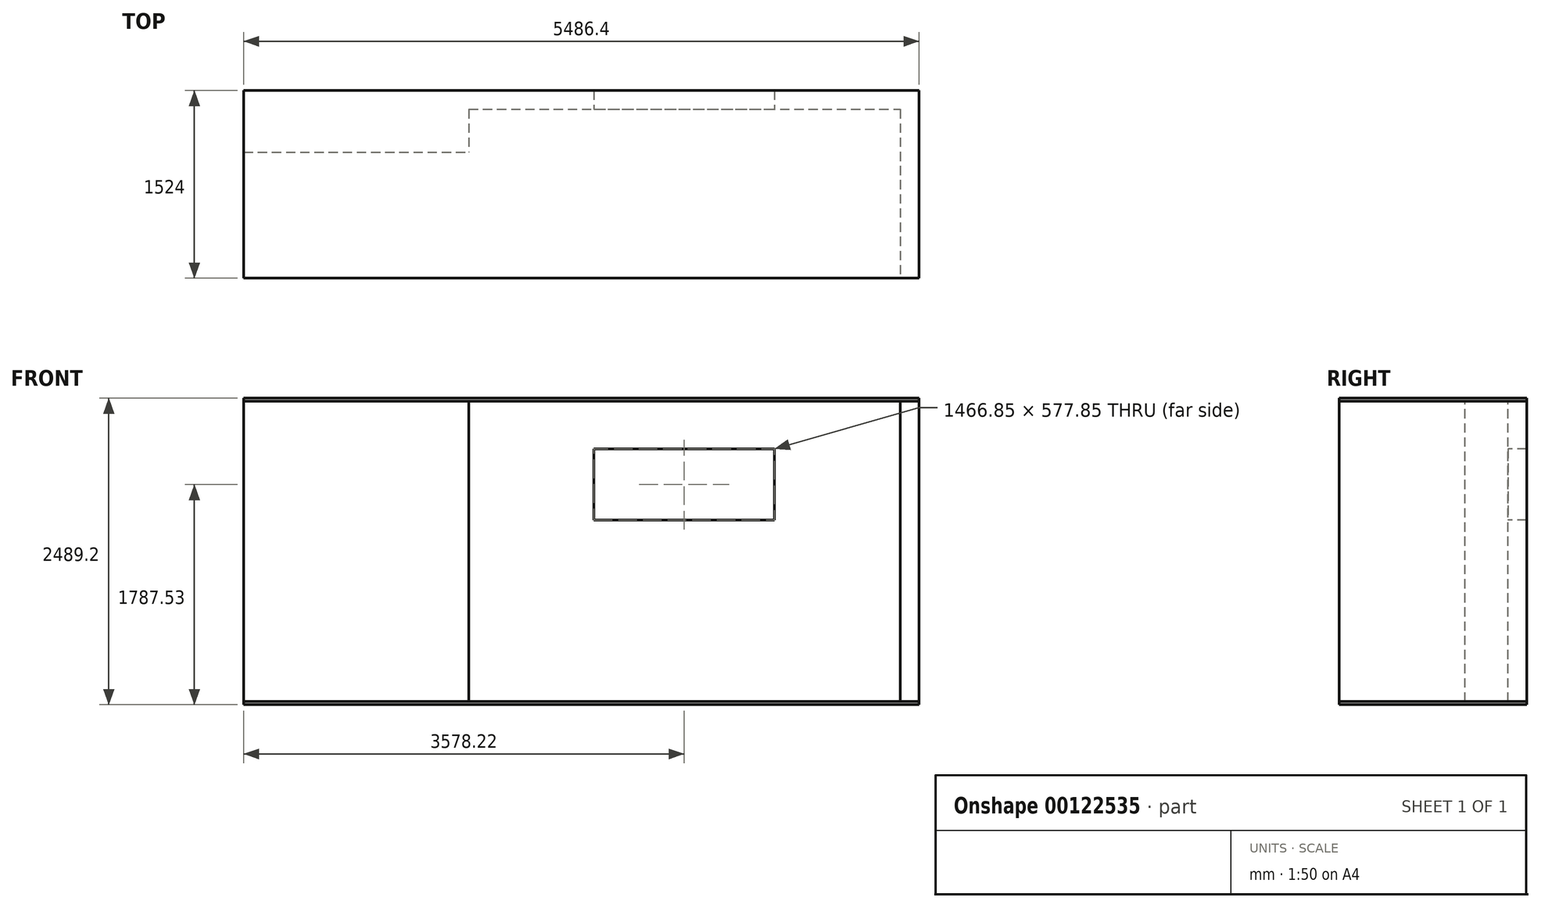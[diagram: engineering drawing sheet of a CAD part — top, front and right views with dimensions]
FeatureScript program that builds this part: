
annotation { "Feature Type Name" : "Feature", "Feature Type Description" : "" }
export const myFeature = defineFeature(function(context is Context, id is Id, definition is map)
    precondition{}
    {
        {
            var Q0;
            Q0=qCreatedBy(makeId("Front.planeOp"),FACE);
            var sketch = newSketch(context, id + "F0", { "sketchPlane" : qUnion([Q0])});
            skLineSegment(sketch, "E0.bottom", {"start": v(0, 0) * mm, "end": v(3505.2, 0) * mm});
            skLineSegment(sketch, "E0.top", {"start": v(0, 2438.4) * mm, "end": v(3505.2, 2438.4) * mm});
            skLineSegment(sketch, "E0.left", {"start": v(0, 0) * mm, "end": v(0, 2438.4) * mm});
            skLineSegment(sketch, "E0.right", {"start": v(3505.2, 0) * mm, "end": v(3505.2, 2438.4) * mm});
            skLineSegment(sketch, "E1.bottom", {"start": v(1016, 2051.05) * mm, "end": v(2482.85, 2051.05) * mm});
            skLineSegment(sketch, "E1.top", {"start": v(1016, 1473.2) * mm, "end": v(2482.85, 1473.2) * mm});
            skLineSegment(sketch, "E1.left", {"start": v(1016, 2051.05) * mm, "end": v(1016, 1473.2) * mm});
            skLineSegment(sketch, "E1.right", {"start": v(2482.85, 2051.05) * mm, "end": v(2482.85, 1473.2) * mm});
            skSolve(sketch);
        }
        {
            var Q0;
            Q0=makeQuery(id+"F0.imprint","IMPRINT",FACE,{"disambiguationData":[TD([[makeQuery(id+"F0.imprint","IMPRINT",EDGE,{"derivedFrom":sQuery(id+"F0.wireOp",EDGE,"E0.bottom")}),1.0]])]});
            extrude(context, id + "F1", {"entities" : qUnion([Q0]), "oppositeDirection" : true, "depth" : 152.4 * mm});
        }
        {
            var Q0;
            Q0=qCreatedBy(makeId("Right.planeOp"),FACE);
            var sketch = newSketch(context, id + "F2", { "sketchPlane" : qUnion([Q0])});
            skLineSegment(sketch, "E2.bottom", {"start": v(0, 0) * mm, "end": v(-349.25, 0) * mm});
            skLineSegment(sketch, "E2.top", {"start": v(0, 2438.4) * mm, "end": v(-349.25, 2438.4) * mm});
            skLineSegment(sketch, "E2.left", {"start": v(0, 0) * mm, "end": v(0, 2438.4) * mm});
            skLineSegment(sketch, "E2.right", {"start": v(-349.25, 0) * mm, "end": v(-349.25, 2438.4) * mm});
            skSolve(sketch);
        }
        {
            var Q0;
            Q0=makeQuery(id+"F2.imprint","IMPRINT",FACE,{"disambiguationData":[TD([[makeQuery(id+"F2.imprint","IMPRINT",EDGE,{"derivedFrom":sQuery(id+"F2.wireOp",EDGE,"E2.bottom")}),-1.0]])]});
            var Q1;
            Q1=makeQuery(id+"F1.opExtrude","SWEPT_FACE",FACE,{"disambiguationData":[OSD([sQuery(id+"F0.wireOp",EDGE,"E0.left")])]});
            extrude(context, id + "F3", {"entities" : qUnion([Q0, Q1]), "operationType" : NewBodyOperationType.ADD, "oppositeDirection" : true, "depth" : 1828.8 * mm});
        }
        {
            var Q0;
            Q0=makeQuery(id+"F1.opExtrude","SWEPT_FACE",FACE,{"disambiguationData":[OSD([sQuery(id+"F0.wireOp",EDGE,"E0.right")])]});
            var sketch = newSketch(context, id + "F4", { "sketchPlane" : qUnion([Q0])});
            skLineSegment(sketch, "E3.bottom", {"start": v(152.4, 0) * mm, "end": v(-1371.6, 0) * mm});
            skLineSegment(sketch, "E3.top", {"start": v(152.4, 2438.4) * mm, "end": v(-1371.6, 2438.4) * mm});
            skLineSegment(sketch, "E3.left", {"start": v(152.4, 0) * mm, "end": v(152.4, 2438.4) * mm});
            skLineSegment(sketch, "E3.right", {"start": v(-1371.6, 0) * mm, "end": v(-1371.6, 2438.4) * mm});
            skSolve(sketch);
        }
        {
            var Q0;
            {var subQ2=sQuery(id+"F4.wireOp",EDGE,"E3.right");Q0=makeQuery(id+"F4.imprint","IMPRINT",FACE,{"disambiguationData":[TD([[makeQuery(id+"F4.imprint","IMPRINT",EDGE,{"derivedFrom":subQ2}),-1.0]])]});}
            var Q1;
            {var subQ2=sQuery(id+"F4.wireOp",EDGE,"E3.left");Q1=makeQuery(id+"F4.imprint","IMPRINT",FACE,{"disambiguationData":[TD([[makeQuery(id+"F4.imprint","IMPRINT",EDGE,{"derivedFrom":subQ2}),1.0]])]});}
            extrude(context, id + "F5", {"entities" : qUnion([Q0, Q1]), "operationType" : NewBodyOperationType.ADD, "depth" : 152.4 * mm});
        }
        {
            var Q0;
            {var subQ0=sQuery(id+"F0.wireOp",EDGE,"E0.top");Q0=makeQuery(id+"F5.boolean.opBoolean","MERGE",FACE,{"derivedFrom":[makeQuery(id+"F3.boolean.opBoolean","MERGE",FACE,{"derivedFrom":[makeQuery(id+"F1.opExtrude","SWEPT_FACE",FACE,{"disambiguationData":[OSD([subQ0])]}),makeQuery(id+"F3.opExtrude","SWEPT_FACE",FACE,{"disambiguationData":[OSD([subQ0,sQuery(id+"F0.wireOp",EDGE,"E0.left")])]}),makeQuery(id+"F3.opExtrude","SWEPT_FACE",FACE,{"disambiguationData":[OSD([sQuery(id+"F2.wireOp",EDGE,"E2.top")])]})]}),makeQuery(id+"F5.opExtrude","SWEPT_FACE",FACE,{"disambiguationData":[OSD([sQuery(id+"F4.wireOp",EDGE,"E3.top")])]})]});}
            var sketch = newSketch(context, id + "F6", { "sketchPlane" : qUnion([Q0])});
            skLineSegment(sketch, "E4.0", {"start": v(3657.6, 152.4) * mm, "end": v(3657.6, -1371.6) * mm});
            skLineSegment(sketch, "E4.1", {"start": v(-1828.8, 152.4) * mm, "end": v(3657.6, 152.4) * mm});
            skLineSegment(sketch, "E5", {"start": v(-1828.8, 152.4) * mm, "end": v(-1828.8, -1371.6) * mm});
            skLineSegment(sketch, "E6", {"start": v(3657.6, -1371.6) * mm, "end": v(-1828.8, -1371.6) * mm});
            skSolve(sketch);
        }
        {
            var Q0;
            {var subQ6=sQuery(id+"F0.wireOp",EDGE,"E0.top");Q0=makeQuery(id+"F6.imprint","IMPRINT",FACE,{"disambiguationData":[TD([[makeQuery(id+"F6.imprint","IMPRINT",EDGE,{"derivedFrom":makeQuery(id+"F1.opExtrude","CAP_EDGE",EDGE,{"disambiguationData":[OSD([subQ6])],"isStart":true})}),-1.0]])]});}
            var Q1;
            {var subQ6=sQuery(id+"F6.wireOp",EDGE,"E4.0");Q1=makeQuery(id+"F6.imprint","IMPRINT",FACE,{"disambiguationData":[TD([[makeQuery(id+"F6.imprint","IMPRINT",EDGE,{"derivedFrom":subQ6}),-1.0]])]});}
            extrude(context, id + "F7", {"entities" : qUnion([Q0, Q1]), "depth" : 25.4 * mm});
        }
        {
            var Q0;
            Q0=qCreatedBy(makeId("Top.planeOp"),FACE);
            var sketch = newSketch(context, id + "F8", { "sketchPlane" : qUnion([Q0])});
            skLineSegment(sketch, "E7.0.0", {"start": v(-1828.8, -1371.6) * mm, "end": v(3657.6, -1371.6) * mm});
            skLineSegment(sketch, "E7.0.1", {"start": v(3657.6, -1371.6) * mm, "end": v(3657.6, 152.4) * mm});
            skLineSegment(sketch, "E7.0.2", {"start": v(3657.6, 152.4) * mm, "end": v(-1828.8, 152.4) * mm});
            skLineSegment(sketch, "E7.0.3", {"start": v(-1828.8, 152.4) * mm, "end": v(-1828.8, -1371.6) * mm});
            skSolve(sketch);
        }
        {
            var Q0;
            Q0=makeQuery(id+"F8.imprint","IMPRINT",FACE,{"disambiguationData":[TD([[makeQuery(id+"F8.imprint","IMPRINT",EDGE,{"derivedFrom":sQuery(id+"F8.wireOp",EDGE,"E7.0.0")}),1.0]])]});
            extrude(context, id + "F9", {"entities" : qUnion([Q0]), "oppositeDirection" : true, "depth" : 25.4 * mm});
        }
    });
